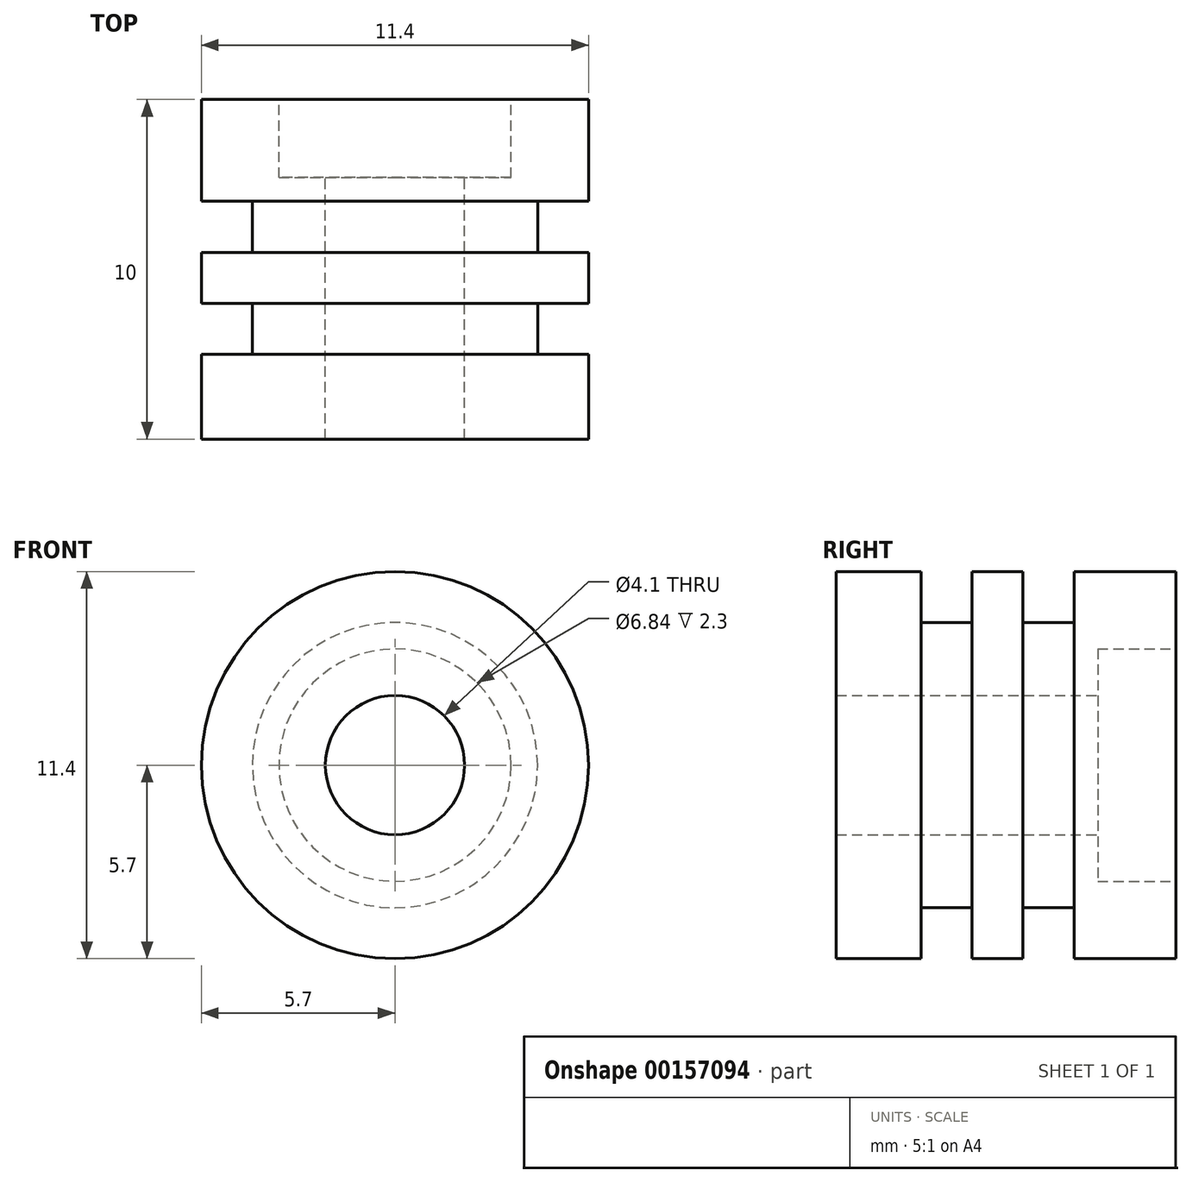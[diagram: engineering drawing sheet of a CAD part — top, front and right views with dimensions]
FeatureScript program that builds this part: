
annotation { "Feature Type Name" : "Feature", "Feature Type Description" : "" }
export const myFeature = defineFeature(function(context is Context, id is Id, definition is map)
    precondition{}
    {
        {
            var Q0;
            Q0=qCreatedBy(makeId("Right.planeOp"),FACE);
            var sketch = newSketch(context, id + "F0", { "sketchPlane" : qUnion([Q0])});
            skLineSegment(sketch, "E0", {"start": v(11.47, 0) * mm, "end": v(0, 0) * mm, "construction": true});
            skLineSegment(sketch, "E1", {"start": v(7.7, 2.05) * mm, "end": v(0, 2.05) * mm});
            skLineSegment(sketch, "E2", {"start": v(7.7, 2.05) * mm, "end": v(7.7, 3.42) * mm});
            skLineSegment(sketch, "E3", {"start": v(10, 3.42) * mm, "end": v(7.7, 3.42) * mm});
            skLineSegment(sketch, "E4", {"start": v(10, 3.42) * mm, "end": v(10, 5.7) * mm});
            skLineSegment(sketch, "E5", {"start": v(7, 5.7) * mm, "end": v(10, 5.7) * mm});
            skLineSegment(sketch, "E6", {"start": v(7, 5.7) * mm, "end": v(7, 4.2) * mm});
            skLineSegment(sketch, "E7", {"start": v(5.5, 4.2) * mm, "end": v(7, 4.2) * mm});
            skLineSegment(sketch, "E8", {"start": v(2.5, 4.2) * mm, "end": v(2.5, 5.7) * mm});
            skLineSegment(sketch, "E9", {"start": v(0, 5.7) * mm, "end": v(2.5, 5.7) * mm});
            skLineSegment(sketch, "E10", {"start": v(0, 5.7) * mm, "end": v(0, 2.05) * mm});
            skLineSegment(sketch, "E11", {"start": v(4, 4.2) * mm, "end": v(4, 5.7) * mm});
            skLineSegment(sketch, "E12", {"start": v(4, 5.7) * mm, "end": v(5.5, 5.7) * mm});
            skLineSegment(sketch, "E13", {"start": v(5.5, 5.7) * mm, "end": v(5.5, 4.2) * mm});
            skLineSegment(sketch, "E14.trimOffspring", {"start": v(4, 4.2) * mm, "end": v(2.5, 4.2) * mm});
            skSolve(sketch);
        }
        {
            var Q0;
            Q0=makeQuery(id+"F0.imprint","IMPRINT",FACE,{"disambiguationData":[TD([[makeQuery(id+"F0.imprint","IMPRINT",EDGE,{"derivedFrom":sQuery(id+"F0.wireOp",EDGE,"E1")}),-1.0]])]});
            var Q1;
            Q1=sQuery(id+"F0.wireOp",EDGE,"E0");
            revolve(context, id + "F1", {"entities" : qUnion([Q0]), "axis" : qUnion([Q1]), "revolveType" : RevolveType.FULL});
        }
    });
